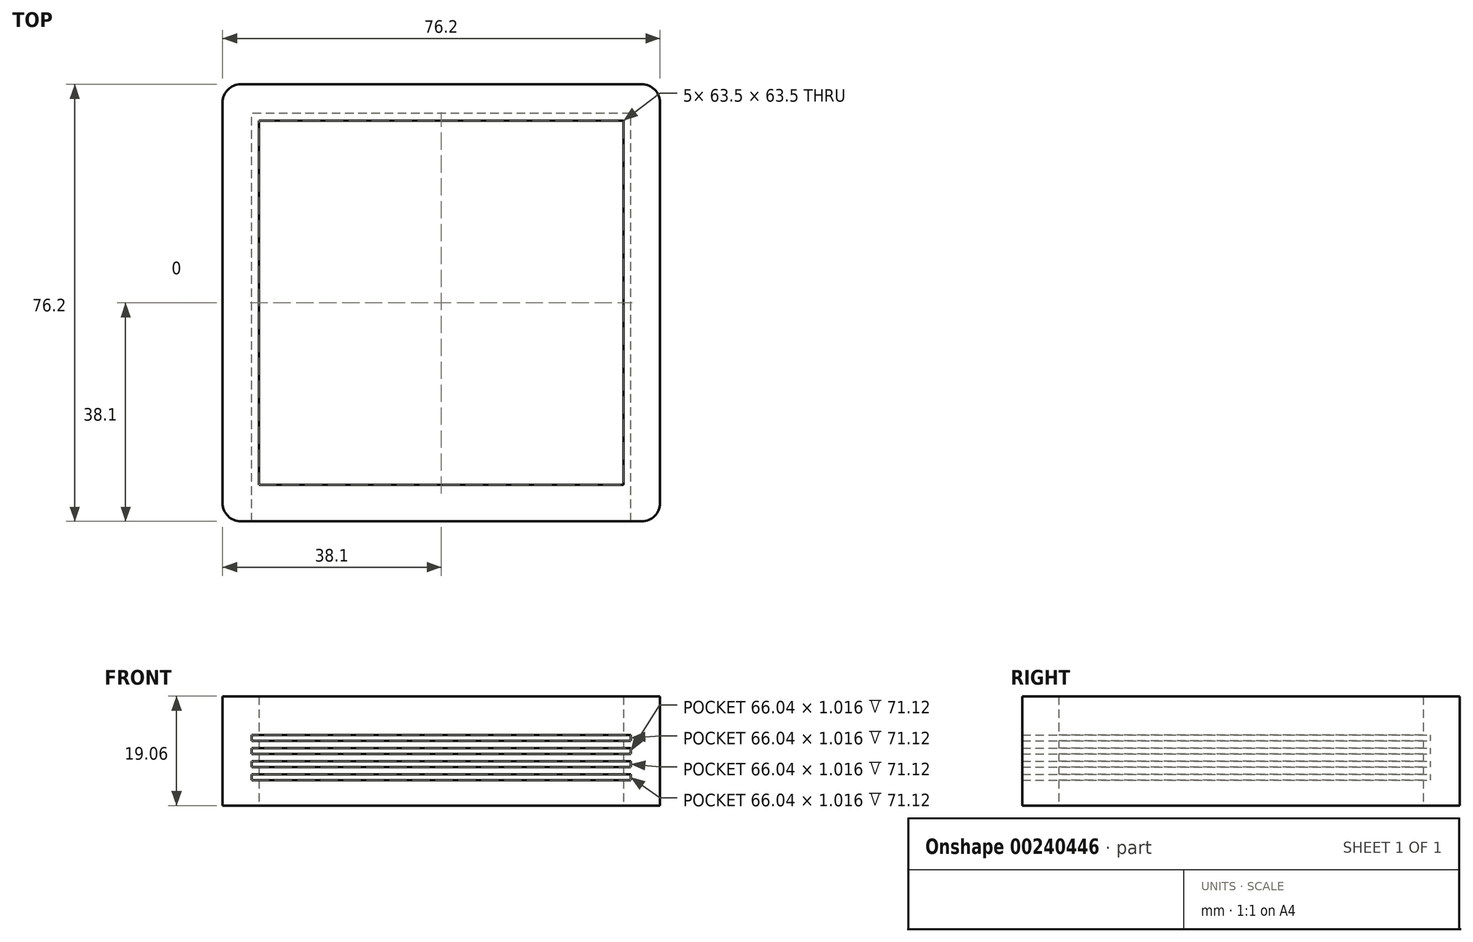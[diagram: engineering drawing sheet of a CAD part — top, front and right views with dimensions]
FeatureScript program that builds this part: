
annotation { "Feature Type Name" : "Feature", "Feature Type Description" : "" }
export const myFeature = defineFeature(function(context is Context, id is Id, definition is map)
    precondition{}
    {
        {
            var Q0;
            Q0=qCreatedBy(makeId("Top.planeOp"),FACE);
            var sketch = newSketch(context, id + "F0", { "sketchPlane" : qUnion([Q0])});
            skLineSegment(sketch, "E0.bottom", {"start": v(31.75, -31.75) * mm, "end": v(-31.75, -31.75) * mm});
            skLineSegment(sketch, "E0.top", {"start": v(31.75, 31.75) * mm, "end": v(-31.75, 31.75) * mm});
            skLineSegment(sketch, "E0.left", {"start": v(31.75, -31.75) * mm, "end": v(31.75, 31.75) * mm});
            skLineSegment(sketch, "E0.right", {"start": v(-31.75, -31.75) * mm, "end": v(-31.75, 31.75) * mm});
            skPoint(sketch, "E0.middle", {"position": v(0, 0) * mm});
            skLineSegment(sketch, "E1.0", {"start": v(38.1, 38.1) * mm, "end": v(-38.1, 38.1) * mm});
            skLineSegment(sketch, "E1.1", {"start": v(38.1, -38.1) * mm, "end": v(38.1, 38.1) * mm});
            skLineSegment(sketch, "E1.2", {"start": v(38.1, -38.1) * mm, "end": v(-38.1, -38.1) * mm});
            skLineSegment(sketch, "E1.3", {"start": v(-38.1, -38.1) * mm, "end": v(-38.1, 38.1) * mm});
            skSolve(sketch);
        }
        {
            var Q0;
            Q0 = qSketchRegion(id + "F0", true);
            extrude(context, id + "F1", {"entities" : qUnion([Q0]), "endBound" : BoundingType.SYMMETRIC, "depth" : 19.05 * mm});
        }
        {
            var Q0;
            Q0=qCreatedBy(makeId("Front.planeOp"),FACE);
            var sketch = newSketch(context, id + "F2", { "sketchPlane" : qUnion([Q0])});
            skLineSegment(sketch, "E2.bottom", {"start": v(33.02, -0.5) * mm, "end": v(-33.02, -0.5) * mm});
            skLineSegment(sketch, "E2.top", {"start": v(33.02, 0.5) * mm, "end": v(-33.02, 0.5) * mm});
            skLineSegment(sketch, "E2.left", {"start": v(33.02, -0.5) * mm, "end": v(33.02, 0.5) * mm});
            skLineSegment(sketch, "E2.right", {"start": v(-33.02, -0.5) * mm, "end": v(-33.02, 0.5) * mm});
            skPoint(sketch, "E2.middle", {"position": v(0, 0) * mm});
            skLineSegment(sketch, "E3.bottom", {"start": v(33.02, 1.78) * mm, "end": v(-33.02, 1.78) * mm});
            skLineSegment(sketch, "E3.top", {"start": v(33.02, 2.8) * mm, "end": v(-33.02, 2.8) * mm});
            skLineSegment(sketch, "E3.left", {"start": v(33.02, 1.78) * mm, "end": v(33.02, 2.8) * mm});
            skLineSegment(sketch, "E3.right", {"start": v(-33.02, 1.78) * mm, "end": v(-33.02, 2.8) * mm});
            skLineSegment(sketch, "E4.bottom", {"start": v(33.02, -2.8) * mm, "end": v(-33.02, -2.8) * mm});
            skLineSegment(sketch, "E4.top", {"start": v(33.02, -1.78) * mm, "end": v(-33.02, -1.78) * mm});
            skLineSegment(sketch, "E4.left", {"start": v(33.02, -2.8) * mm, "end": v(33.02, -1.78) * mm});
            skLineSegment(sketch, "E4.right", {"start": v(-33.02, -2.8) * mm, "end": v(-33.02, -1.78) * mm});
            skLineSegment(sketch, "E5.bottom", {"start": v(33.02, -5.08) * mm, "end": v(-33.02, -5.08) * mm});
            skLineSegment(sketch, "E5.top", {"start": v(33.02, -4.06) * mm, "end": v(-33.02, -4.06) * mm});
            skLineSegment(sketch, "E5.left", {"start": v(33.02, -5.08) * mm, "end": v(33.02, -4.06) * mm});
            skLineSegment(sketch, "E5.right", {"start": v(-33.02, -5.08) * mm, "end": v(-33.02, -4.06) * mm});
            skSolve(sketch);
        }
        {
            var Q0;
            Q0 = qSketchRegion(id + "F2", true);
            var Q1;
            Q1=makeQuery(id+"F1.opExtrude","SWEPT_FACE",FACE,{"disambiguationData":[OSD([sQuery(id+"F0.wireOp",EDGE,"E1.2")])]});
            extrude(context, id + "F3", {"entities" : qUnion([Q0]), "operationType" : NewBodyOperationType.REMOVE, "endBound" : BoundingType.UP_TO_SURFACE, "endBoundEntityFace" : qUnion([Q1]), "depth" : 25.4 * mm});
        }
        {
            var Q0;
            Q0 = qSketchRegion(id + "F2", true);
            extrude(context, id + "F4", {"entities" : qUnion([Q0]), "operationType" : NewBodyOperationType.REMOVE, "oppositeDirection" : true, "depth" : 31.75 * mm});
        }
        {
            var Q0;
            Q0=makeQuery(id+"F1.opExtrude","SWEPT_EDGE",EDGE,{"disambiguationData":[OSD([sQuery(id+"F0.wireOp",EDGE,"E1.2"),sQuery(id+"F0.wireOp",EDGE,"E1.3")])]});
            var Q1;
            Q1=makeQuery(id+"F1.opExtrude","SWEPT_EDGE",EDGE,{"disambiguationData":[OSD([sQuery(id+"F0.wireOp",EDGE,"E1.1"),sQuery(id+"F0.wireOp",EDGE,"E1.2")])]});
            var Q2;
            Q2=makeQuery(id+"F1.opExtrude","SWEPT_EDGE",EDGE,{"disambiguationData":[OSD([sQuery(id+"F0.wireOp",EDGE,"E1.0"),sQuery(id+"F0.wireOp",EDGE,"E1.1")])]});
            var Q3;
            Q3=makeQuery(id+"F1.opExtrude","SWEPT_EDGE",EDGE,{"disambiguationData":[OSD([sQuery(id+"F0.wireOp",EDGE,"E1.0"),sQuery(id+"F0.wireOp",EDGE,"E1.3")])]});
            fillet(context, id + "F5", {"entities" : qUnion([Q0, Q1, Q2, Q3]), "radius" : 3.17 * mm, "tangentPropagation" : true, "allowEdgeOverflow" : false});
        }
        {
            var Q0;
            Q0 = qSketchRegion(id + "F2", true);
            extrude(context, id + "F6", {"entities" : qUnion([Q0]), "operationType" : NewBodyOperationType.REMOVE, "oppositeDirection" : true, "depth" : 33.02 * mm});
        }
    });
